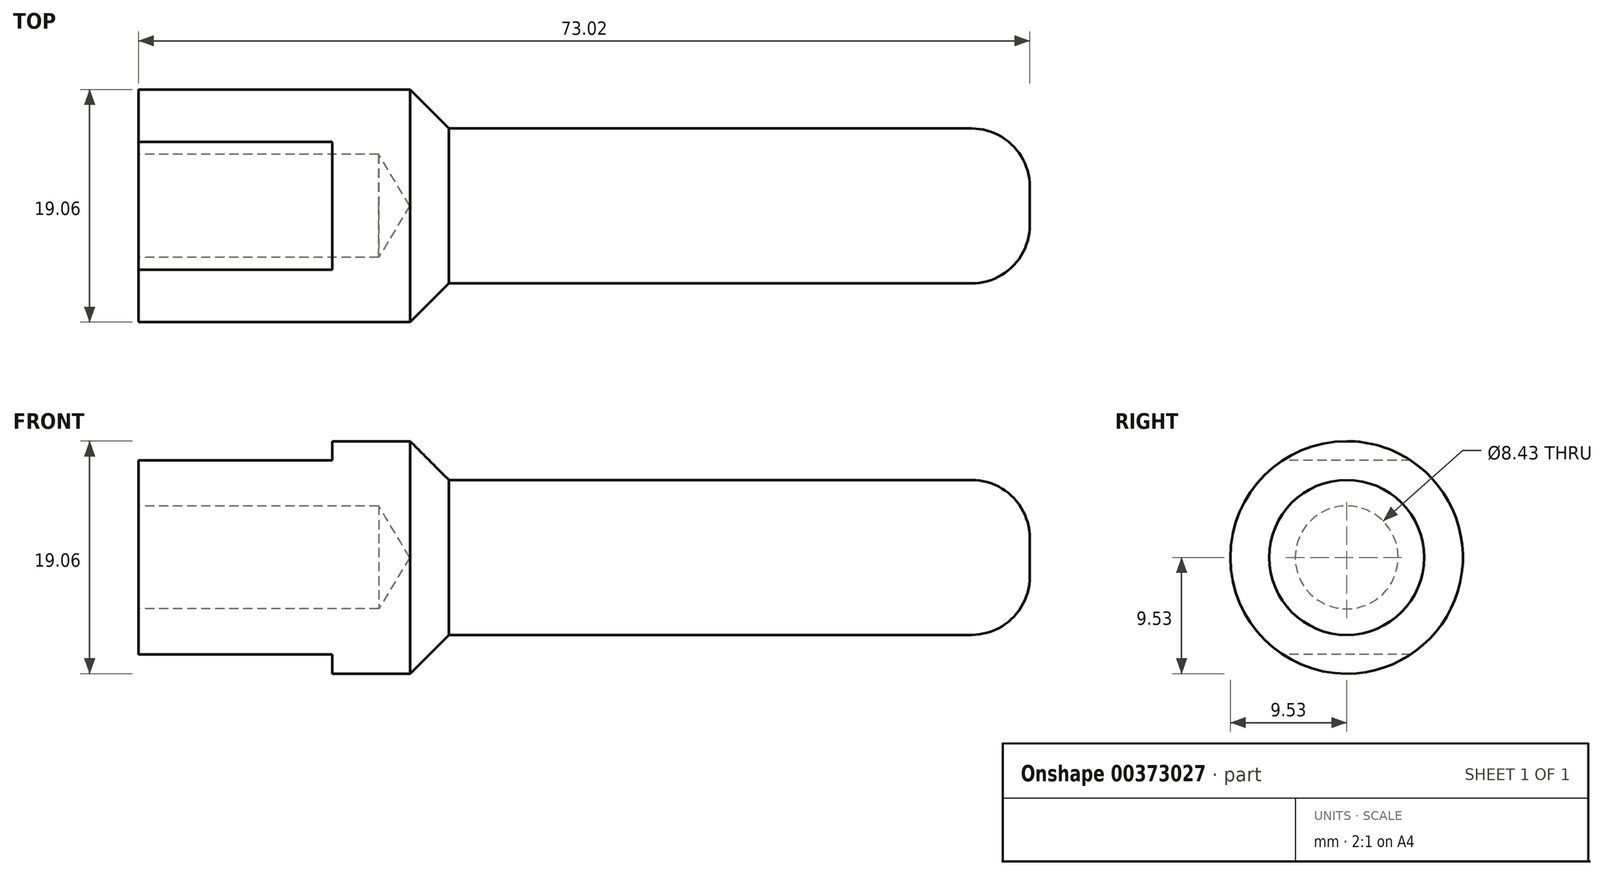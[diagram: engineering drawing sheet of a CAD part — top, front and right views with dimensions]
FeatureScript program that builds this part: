
annotation { "Feature Type Name" : "Feature", "Feature Type Description" : "" }
export const myFeature = defineFeature(function(context is Context, id is Id, definition is map)
    precondition{}
    {
        {
            var Q0;
            Q0=qCreatedBy(makeId("Top.planeOp"),FACE);
            var sketch = newSketch(context, id + "F0", { "sketchPlane" : qUnion([Q0])});
            skLineSegment(sketch, "E0", {"start": v(-24.61, 0) * mm, "end": v(48.41, 0) * mm});
            skLineSegment(sketch, "E1", {"start": v(-24.61, 0) * mm, "end": v(-24.61, 9.53) * mm});
            skLineSegment(sketch, "E2", {"start": v(-24.61, 9.53) * mm, "end": v(0.81, 9.53) * mm});
            skLineSegment(sketch, "E3", {"start": v(0.81, 9.53) * mm, "end": v(0.81, 6.35) * mm});
            skLineSegment(sketch, "E4", {"start": v(0.81, 6.35) * mm, "end": v(48.41, 6.35) * mm});
            skLineSegment(sketch, "E5", {"start": v(48.41, 6.35) * mm, "end": v(48.41, 0) * mm});
            skLineSegment(sketch, "E6", {"start": v(-9.17, 9.53) * mm, "end": v(-9.17, 0) * mm});
            skLineSegment(sketch, "E7", {"start": v(-9.17, 9.53) * mm, "end": v(-9.17, 13.8) * mm});
            skSolve(sketch);
        }
        {
            var Q0;
            {var subQ0=sQuery(id+"F0.wireOp",EDGE,"E1");Q0=makeQuery(id+"F0.imprint","IMPRINT",FACE,{"disambiguationData":[TD([[makeQuery(id+"F0.imprint","IMPRINT",EDGE,{"derivedFrom":subQ0}),-1.0]])]});}
            var Q1;
            {var subQ0=sQuery(id+"F0.wireOp",EDGE,"E3");Q1=makeQuery(id+"F0.imprint","IMPRINT",FACE,{"disambiguationData":[TD([[makeQuery(id+"F0.imprint","IMPRINT",EDGE,{"derivedFrom":subQ0}),-1.0]])]});}
            var Q2;
            Q2=sQuery(id+"F0.wireOp",EDGE,"E0");
            revolve(context, id + "F1", {"surfaceOperationType" : NewSurfaceOperationType.NEW, "entities" : qUnion([Q0, Q1]), "axis" : qUnion([Q2]), "revolveType" : RevolveType.FULL});
        }
        {
            var Q0;
            Q0=makeQuery(id+"F1.opRevolve","SWEPT_FACE",FACE,{"disambiguationData":[OSD([sQuery(id+"F0.wireOp",EDGE,"E1")])]});
            var sketch = newSketch(context, id + "F2", { "sketchPlane" : qUnion([Q0])});
            skLineSegment(sketch, "E8", {"start": v(-9.53, 0) * mm, "end": v(9.53, 0) * mm});
            skLineSegment(sketch, "E9.0", {"start": v(-9.53, -7.94) * mm, "end": v(9.53, -7.94) * mm});
            skLineSegment(sketch, "E10.0", {"start": v(-9.53, 7.95) * mm, "end": v(9.53, 7.95) * mm});
            skSolve(sketch);
        }
        {
            var Q0;
            {var subQ0=sQuery(id+"F2.wireOp",EDGE,"E10.0");var subQ1=makeQuery(id+"F1.opRevolve","SWEPT_EDGE",EDGE,{"disambiguationData":[OSD([sQuery(id+"F0.wireOp",EDGE,"E1"),sQuery(id+"F0.wireOp",EDGE,"E2")])]});var subQ2=makeQuery(id+"F2.imprint","INTERSECT",VERTEX,{"disambiguationData":[OD(0.0)],"derivedFrom":[subQ1,subQ0]});Q0=makeQuery(id+"F2.imprint","IMPRINT",FACE,{"disambiguationData":[TD([[makeQuery(id+"F2.imprint","IMPRINT",EDGE,{"disambiguationData":[TD([[subQ2,-1.0]])],"derivedFrom":subQ0}),1.0]])]});}
            var Q1;
            {var subQ0=sQuery(id+"F2.wireOp",EDGE,"E9.0");var subQ1=makeQuery(id+"F1.opRevolve","SWEPT_EDGE",EDGE,{"disambiguationData":[OSD([sQuery(id+"F0.wireOp",EDGE,"E1"),sQuery(id+"F0.wireOp",EDGE,"E2")])]});var subQ2=makeQuery(id+"F2.imprint","INTERSECT",VERTEX,{"disambiguationData":[OD(0.0)],"derivedFrom":[subQ1,subQ0]});Q1=makeQuery(id+"F2.imprint","IMPRINT",FACE,{"disambiguationData":[TD([[makeQuery(id+"F2.imprint","IMPRINT",EDGE,{"disambiguationData":[TD([[subQ2,-1.0]])],"derivedFrom":subQ0}),-1.0]])]});}
            extrude(context, id + "F3", {"entities" : qUnion([Q0, Q1]), "operationType" : NewBodyOperationType.REMOVE, "oppositeDirection" : true, "depth" : 15.88 * mm, "offsetDistance" : 25.4 * mm});
        }
        {
            var Q0;
            Q0=makeQuery(id+"F1.opRevolve","SWEPT_EDGE",EDGE,{"disambiguationData":[OSD([sQuery(id+"F0.wireOp",EDGE,"E4"),sQuery(id+"F0.wireOp",EDGE,"E5")])]});
            fillet(context, id + "F4", {"entities" : qUnion([Q0]), "radius" : 4.78 * mm, "tangentPropagation" : true, "allowEdgeOverflow" : false});
        }
        {
            var Q0;
            Q0=makeQuery(id+"F1.opRevolve","SWEPT_EDGE",EDGE,{"disambiguationData":[OSD([sQuery(id+"F0.wireOp",EDGE,"E2"),sQuery(id+"F0.wireOp",EDGE,"E3")])]});
            chamfer(context, id + "F5", {"entities" : qUnion([Q0]), "width" : 3.17 * mm, "tangentPropagation" : true});
        }
        {
            var Q0;
            Q0=makeQuery(id+"F1.opRevolve","SWEPT_FACE",FACE,{"disambiguationData":[OSD([sQuery(id+"F0.wireOp",EDGE,"E1")])]});
            var sketch = newSketch(context, id + "F6", { "sketchPlane" : qUnion([Q0])});
            skPoint(sketch, "E11", {"position": v(0, 0) * mm});
            skSolve(sketch);
        }
        {
            var Q0;
            Q0=sQuery(id+"F6.wireOp",VERTEX,"E11");
            var Q1;
            Q1=makeQuery(id+"F1.opRevolve","SWEPT_BODY",BODY,{"disambiguationData":[OSD([sQuery(id+"F0.wireOp",EDGE,"E0"),sQuery(id+"F0.wireOp",EDGE,"E1"),sQuery(id+"F0.wireOp",EDGE,"E2"),sQuery(id+"F0.wireOp",EDGE,"E3"),sQuery(id+"F0.wireOp",EDGE,"E4"),sQuery(id+"F0.wireOp",EDGE,"E5")])]});
            hole(context, id + "F7", {"style" : HoleStyle.SIMPLE, "endStyle" : HoleEndStyle.BLIND, "standardTappedOrClearance" : lookupTablePath({ "standard" : "ANSI", "engagement" : "75%", "pitch" : "24 tpi", "size" : "3/8", "type" : "Tapped" }), "standardBlindInLast" : lookupTablePath({ "standard" : "ANSI", "fit" : "Normal", "engagement" : "75%", "pitch" : "24 tpi", "size" : "3/8", "type" : "Clearance & tapped" }), "holeDiameter" : 8.43 * mm, "majorDiameter" : 9.52 * mm, "showTappedDepth" : true, "holeDepth" : 19.7 * mm, "tappedDepth" : 16.5 * mm, "tapClearance" : 3, "startFromSketch" : true, "locations" : qUnion([Q0]), "scope" : qUnion([Q1])});
        }
    });
